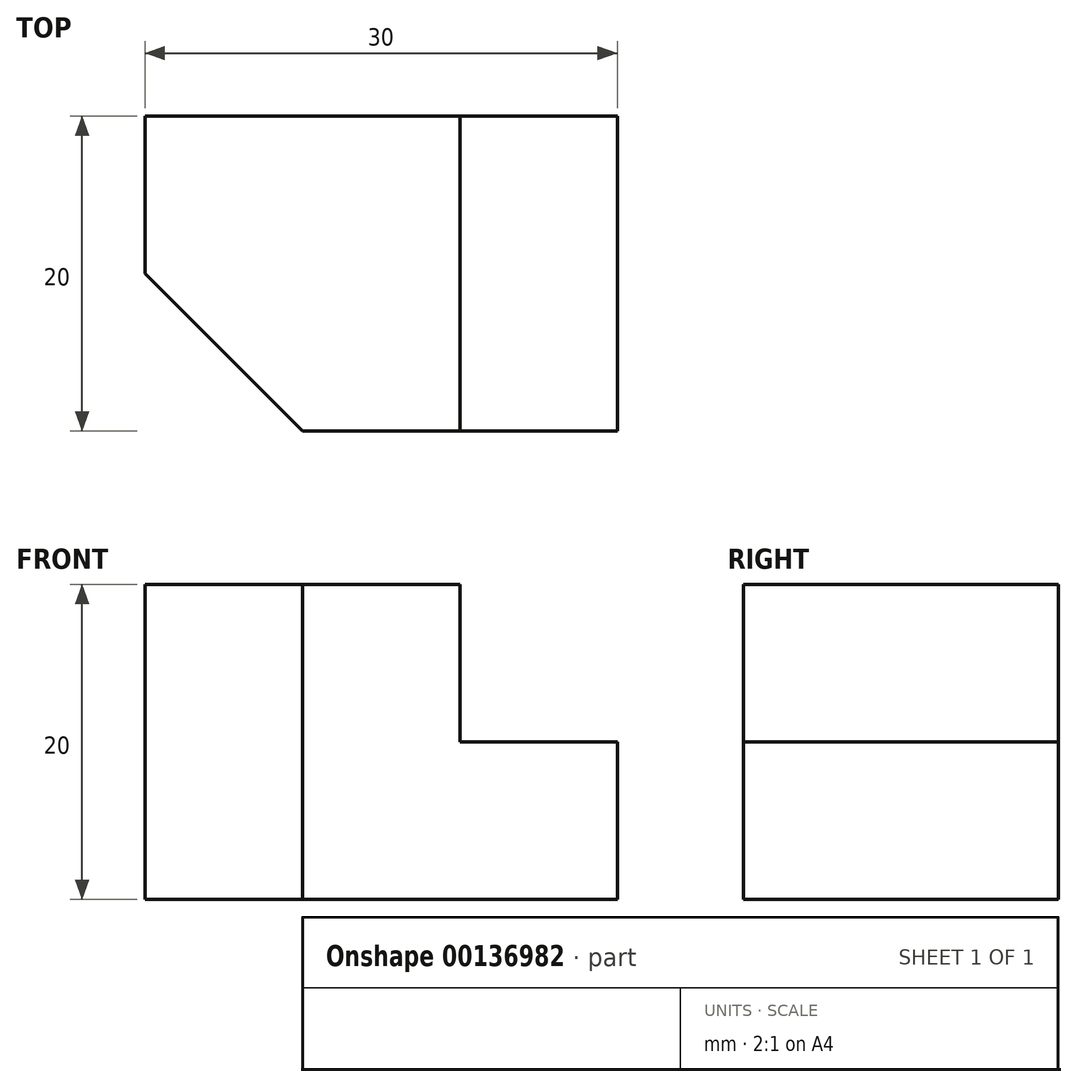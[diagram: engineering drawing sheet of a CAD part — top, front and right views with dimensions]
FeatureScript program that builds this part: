
annotation { "Feature Type Name" : "Feature", "Feature Type Description" : "" }
export const myFeature = defineFeature(function(context is Context, id is Id, definition is map)
    precondition{}
    {
        {
            var Q0;
            Q0=qCreatedBy(makeId("Front.planeOp"),FACE);
            var sketch = newSketch(context, id + "F0", { "sketchPlane" : qUnion([Q0])});
            skLineSegment(sketch, "E0", {"start": v(-15.1, 0) * mm, "end": v(-15.1, 20) * mm});
            skLineSegment(sketch, "E1", {"start": v(-15.1, 20) * mm, "end": v(4.9, 20) * mm});
            skLineSegment(sketch, "E2", {"start": v(4.9, 20) * mm, "end": v(4.9, 10) * mm});
            skLineSegment(sketch, "E3", {"start": v(4.9, 10) * mm, "end": v(14.9, 10) * mm});
            skLineSegment(sketch, "E4", {"start": v(14.9, 10) * mm, "end": v(14.9, 0) * mm});
            skLineSegment(sketch, "E5", {"start": v(14.9, 0) * mm, "end": v(-15.1, 0) * mm});
            skLineSegment(sketch, "E6", {"start": v(-5.1, 20) * mm, "end": v(-5.1, 0) * mm});
            skSolve(sketch);
        }
        {
            var Q0;
            {var subQ1=sQuery(id+"F0.wireOp",EDGE,"E2");Q0=makeQuery(id+"F0.imprint","IMPRINT",FACE,{"disambiguationData":[TD([[makeQuery(id+"F0.imprint","IMPRINT",EDGE,{"derivedFrom":subQ1}),-1.0]])]});}
            var Q1;
            {var subQ0=sQuery(id+"F0.wireOp",EDGE,"E0");Q1=makeQuery(id+"F0.imprint","IMPRINT",FACE,{"disambiguationData":[TD([[makeQuery(id+"F0.imprint","IMPRINT",EDGE,{"derivedFrom":subQ0}),-1.0]])]});}
            extrude(context, id + "F1", {"entities" : qUnion([Q0, Q1]), "depth" : 20 * mm});
        }
        {
            var Q0;
            Q0=qCreatedBy(makeId("Top.planeOp"),FACE);
            var sketch = newSketch(context, id + "F2", { "sketchPlane" : qUnion([Q0])});
            skLineSegment(sketch, "E7", {"start": v(-15.1, -10) * mm, "end": v(-15.1, -20) * mm});
            skLineSegment(sketch, "E8", {"start": v(-15.1, -20) * mm, "end": v(-5.1, -20) * mm});
            skLineSegment(sketch, "E9", {"start": v(-5.1, -20) * mm, "end": v(-15.1, -10) * mm});
            skSolve(sketch);
        }
        {
            var Q0;
            Q0 = qSketchRegion(id + "F2", true);
            extrude(context, id + "F3", {"entities" : qUnion([Q0]), "operationType" : NewBodyOperationType.REMOVE, "depth" : 20 * mm});
        }
    });
